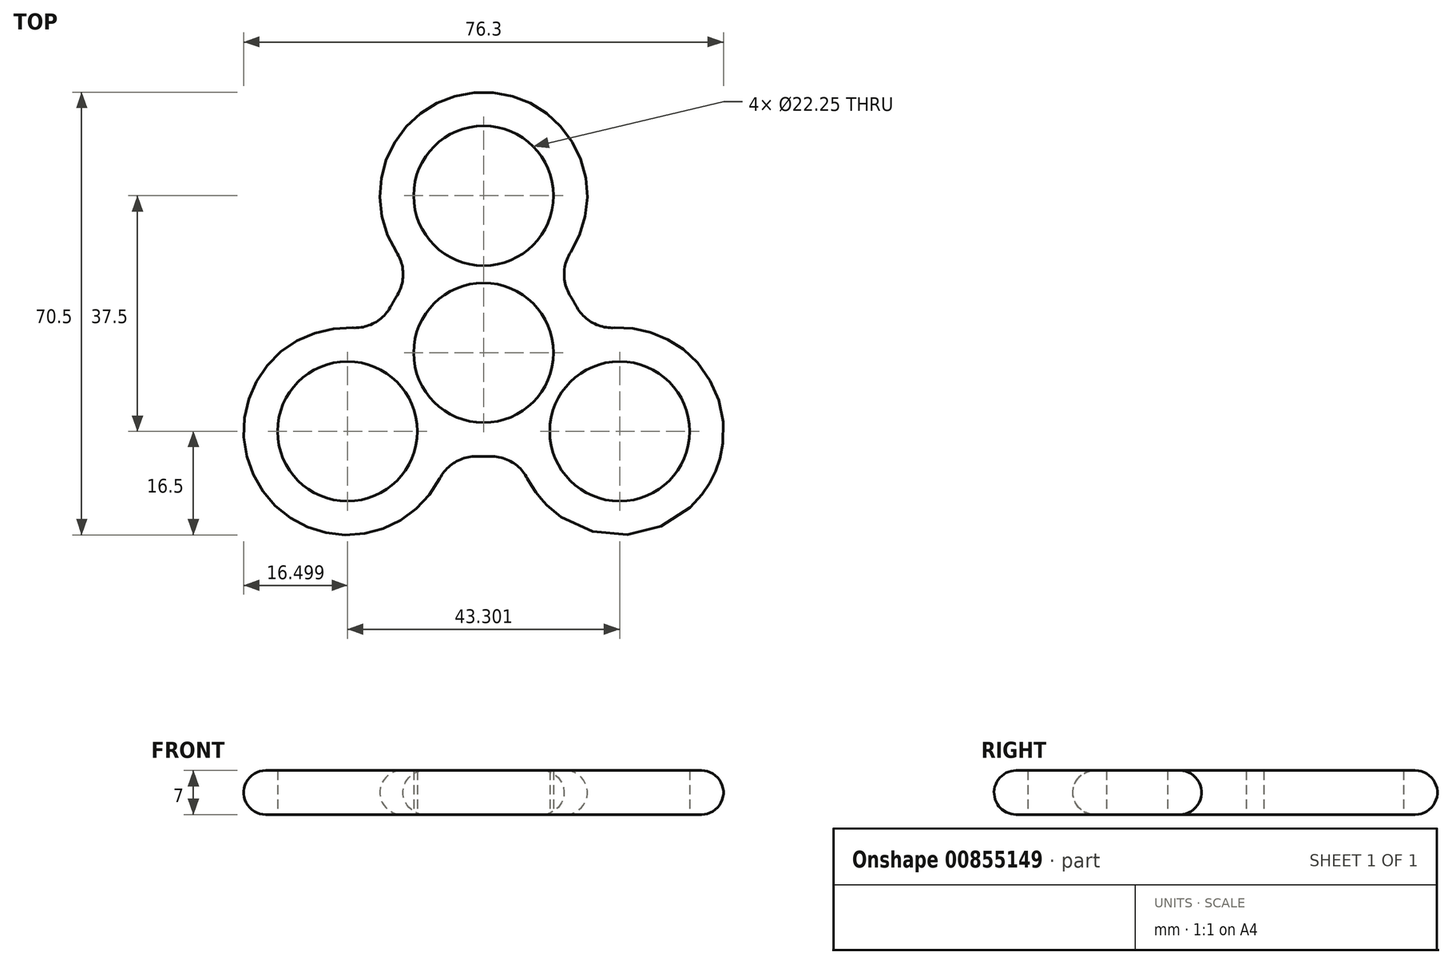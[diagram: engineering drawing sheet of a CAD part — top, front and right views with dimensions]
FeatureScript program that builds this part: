
annotation { "Feature Type Name" : "Feature", "Feature Type Description" : "" }
export const myFeature = defineFeature(function(context is Context, id is Id, definition is map)
    precondition{}
    {
        {
            var Q0;
            Q0=qCreatedBy(makeId("Top.planeOp"),FACE);
            var sketch = newSketch(context, id + "F0", { "sketchPlane" : qUnion([Q0])});
            skCircle(sketch, "E0", {"center": v(0, 0) * mm, "radius": 11.12 * mm});
            skLineSegment(sketch, "E1", {"start": v(0, 0) * mm, "end": v(0, 25) * mm, "construction": true});
            skLineSegment(sketch, "E2", {"start": v(0, 0) * mm, "end": v(-21.65, -12.5) * mm, "construction": true});
            skLineSegment(sketch, "E3", {"start": v(0, 0) * mm, "end": v(21.65, -12.5) * mm, "construction": true});
            skCircle(sketch, "E4", {"center": v(0, 25) * mm, "radius": 11.12 * mm});
            skCircle(sketch, "E5", {"center": v(-21.65, -12.5) * mm, "radius": 11.12 * mm});
            skCircle(sketch, "E6", {"center": v(21.65, -12.5) * mm, "radius": 11.12 * mm});
            skArc(sketch, "E7", {"start": v(10.91, 17.93) * mm, "mid": v(0, 38) * mm, "end": v(-10.91, 17.93) * mm});
            skArc(sketch, "E8", {"start": v(-10.91, 7.07) * mm, "mid": v(-11.26, 6.5) * mm, "end": v(-11.57, 5.92) * mm});
            skArc(sketch, "E9", {"start": v(10.08, -18.42) * mm, "mid": v(32.9, -19) * mm, "end": v(20.99, 0.48) * mm});
            skArc(sketch, "E10", {"start": v(-20.99, 0.48) * mm, "mid": v(-32.9, -19) * mm, "end": v(-10.08, -18.42) * mm});
            skArc(sketch, "E11.trimOffspring", {"start": v(-0.66, -12.98) * mm, "mid": v(0, -13) * mm, "end": v(0.66, -12.98) * mm});
            skArc(sketch, "E12.trimOffspring", {"start": v(11.57, 5.92) * mm, "mid": v(11.26, 6.5) * mm, "end": v(10.91, 7.07) * mm});
            skPoint(sketch, "E13.visualSharp", {"position": v(-3.57, 12.5) * mm});
            skArc(sketch, "E13.filletArc", {"start": v(-10.91, 7.07) * mm, "mid": v(-9.3, 12.5) * mm, "end": v(-10.91, 17.93) * mm});
            skPoint(sketch, "E14.visualSharp", {"position": v(-12.61, -3.16) * mm});
            skArc(sketch, "E14.filletArc", {"start": v(-20.99, 0.48) * mm, "mid": v(-15.48, 1.8) * mm, "end": v(-11.57, 5.92) * mm});
            skPoint(sketch, "E15.visualSharp", {"position": v(-9.04, -9.34) * mm});
            skArc(sketch, "E15.filletArc", {"start": v(-0.66, -12.98) * mm, "mid": v(-6.17, -14.3) * mm, "end": v(-10.08, -18.42) * mm});
            skPoint(sketch, "E16.visualSharp", {"position": v(9.04, -9.34) * mm});
            skArc(sketch, "E16.filletArc", {"start": v(10.08, -18.42) * mm, "mid": v(6.17, -14.3) * mm, "end": v(0.66, -12.98) * mm});
            skPoint(sketch, "E17.visualSharp", {"position": v(12.61, -3.16) * mm});
            skArc(sketch, "E17.filletArc", {"start": v(11.57, 5.92) * mm, "mid": v(15.48, 1.8) * mm, "end": v(20.99, 0.48) * mm});
            skPoint(sketch, "E18.visualSharp", {"position": v(3.57, 12.5) * mm});
            skArc(sketch, "E18.filletArc", {"start": v(10.91, 17.93) * mm, "mid": v(9.3, 12.5) * mm, "end": v(10.91, 7.07) * mm});
            skSolve(sketch);
        }
        {
            var Q0;
            Q0=makeQuery(id+"F0.imprint","IMPRINT",FACE,{"disambiguationData":[TD([[makeQuery(id+"F0.imprint","IMPRINT",EDGE,{"derivedFrom":sQuery(id+"F0.wireOp",EDGE,"E0")}),-1.0]])]});
            extrude(context, id + "F1", {"entities" : qUnion([Q0]), "depth" : 7 * mm, "offsetDistance" : 25 * mm});
        }
        {
            var Q0;
            Q0=qCreatedBy(makeId("Right.planeOp"),FACE);
            var sketch = newSketch(context, id + "F2", { "sketchPlane" : qUnion([Q0])});
            skLineSegment(sketch, "E19", {"start": v(38, 7) * mm, "end": v(38, 0) * mm});
            skArc(sketch, "E20", {"start": v(38, 0) * mm, "mid": v(41.5, 3.5) * mm, "end": v(38, 7) * mm});
            skSolve(sketch);
        }
        {
            var Q0;
            Q0 = qSketchRegion(id + "F2", true);
            var Q1;
            Q1=makeQuery(id+"F2.imprint","IMPRINT",FACE,{"disambiguationData":[TD([[makeQuery(id+"F2.imprint","IMPRINT",EDGE,{"derivedFrom":sQuery(id+"F2.wireOp",EDGE,"E19")}),1.0]])]});
            var Q2;
            Q2=makeQuery(id+"F1.opExtrude","CAP_EDGE",EDGE,{"disambiguationData":[OSD([sQuery(id+"F0.wireOp",EDGE,"E7")])],"isStart":false});
            var Q3;
            Q3=makeQuery(id+"F1.opExtrude","CAP_EDGE",EDGE,{"disambiguationData":[OSD([sQuery(id+"F0.wireOp",EDGE,"E13.filletArc")])],"isStart":false});
            var Q4;
            Q4=makeQuery(id+"F1.opExtrude","CAP_EDGE",EDGE,{"disambiguationData":[OSD([sQuery(id+"F0.wireOp",EDGE,"E8")])],"isStart":false});
            var Q5;
            Q5=makeQuery(id+"F1.opExtrude","CAP_EDGE",EDGE,{"disambiguationData":[OSD([sQuery(id+"F0.wireOp",EDGE,"E14.filletArc")])],"isStart":false});
            var Q6;
            Q6=makeQuery(id+"F1.opExtrude","CAP_EDGE",EDGE,{"disambiguationData":[OSD([sQuery(id+"F0.wireOp",EDGE,"E10")])],"isStart":false});
            var Q7;
            Q7=makeQuery(id+"F1.opExtrude","CAP_EDGE",EDGE,{"disambiguationData":[OSD([sQuery(id+"F0.wireOp",EDGE,"E15.filletArc")])],"isStart":false});
            var Q8;
            Q8=makeQuery(id+"F1.opExtrude","CAP_EDGE",EDGE,{"disambiguationData":[OSD([sQuery(id+"F0.wireOp",EDGE,"E11.trimOffspring")])],"isStart":false});
            var Q9;
            Q9=makeQuery(id+"F1.opExtrude","CAP_EDGE",EDGE,{"disambiguationData":[OSD([sQuery(id+"F0.wireOp",EDGE,"E16.filletArc")])],"isStart":false});
            var Q10;
            Q10=makeQuery(id+"F1.opExtrude","CAP_EDGE",EDGE,{"disambiguationData":[OSD([sQuery(id+"F0.wireOp",EDGE,"E9")])],"isStart":false});
            var Q11;
            Q11=makeQuery(id+"F1.opExtrude","CAP_EDGE",EDGE,{"disambiguationData":[OSD([sQuery(id+"F0.wireOp",EDGE,"E17.filletArc")])],"isStart":false});
            var Q12;
            Q12=makeQuery(id+"F1.opExtrude","CAP_EDGE",EDGE,{"disambiguationData":[OSD([sQuery(id+"F0.wireOp",EDGE,"E12.trimOffspring")])],"isStart":false});
            var Q13;
            Q13=makeQuery(id+"F1.opExtrude","CAP_EDGE",EDGE,{"disambiguationData":[OSD([sQuery(id+"F0.wireOp",EDGE,"E18.filletArc")])],"isStart":false});
            sweep(context, id + "F3", {"operationType" : NewBodyOperationType.ADD, "profiles" : qUnion([Q0, Q1]), "path" : qUnion([Q2, Q3, Q4, Q5, Q6, Q7, Q8, Q9, Q10, Q11, Q12, Q13])});
        }
    });
